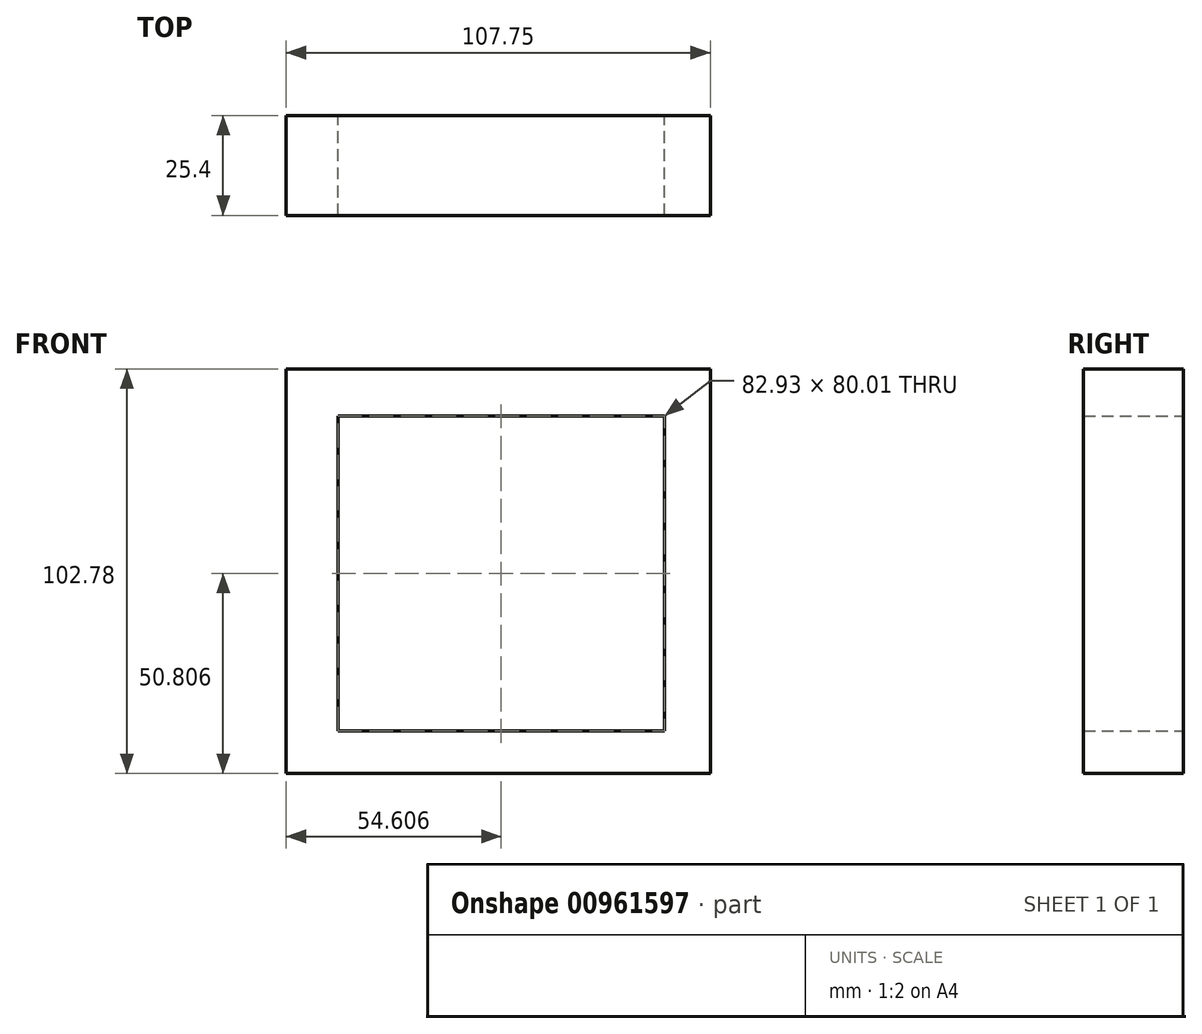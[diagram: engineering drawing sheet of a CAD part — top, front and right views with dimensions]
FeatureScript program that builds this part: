
annotation { "Feature Type Name" : "Feature", "Feature Type Description" : "" }
export const myFeature = defineFeature(function(context is Context, id is Id, definition is map)
    precondition{}
    {
        {
            var Q0;
            Q0=qCreatedBy(makeId("Front.planeOp"),FACE);
            var sketch = newSketch(context, id + "F0", { "sketchPlane" : qUnion([Q0])});
            skLineSegment(sketch, "E0.bottom", {"start": v(0, 55.04) * mm, "end": v(-55.92, 55.04) * mm});
            skLineSegment(sketch, "E0.top", {"start": v(0, -47.74) * mm, "end": v(-55.92, -47.74) * mm});
            skLineSegment(sketch, "E0.left", {"start": v(0, 55.04) * mm, "end": v(0, -47.74) * mm});
            skLineSegment(sketch, "E0.right", {"start": v(-55.92, 55.04) * mm, "end": v(-55.92, -47.74) * mm});
            skPoint(sketch, "E1.oppositeSnap0", {"position": v(-27.96, -47.74) * mm});
            skLineSegment(sketch, "E1.bottom", {"start": v(0, 55.04) * mm, "end": v(51.83, 55.04) * mm});
            skLineSegment(sketch, "E1.top", {"start": v(0, -47.74) * mm, "end": v(51.83, -47.74) * mm});
            skLineSegment(sketch, "E1.right", {"start": v(51.83, 55.04) * mm, "end": v(51.83, -47.74) * mm});
            skLineSegment(sketch, "E2.bottom", {"start": v(0, 43.07) * mm, "end": v(-42.78, 43.07) * mm});
            skLineSegment(sketch, "E2.top", {"start": v(0, -36.94) * mm, "end": v(-42.78, -36.94) * mm});
            skLineSegment(sketch, "E2.left", {"start": v(0, 43.07) * mm, "end": v(0, -36.94) * mm});
            skLineSegment(sketch, "E2.right", {"start": v(-42.78, 43.07) * mm, "end": v(-42.78, -36.94) * mm});
            skLineSegment(sketch, "E3.bottom", {"start": v(0, 43.07) * mm, "end": v(40.15, 43.07) * mm});
            skLineSegment(sketch, "E3.top", {"start": v(0, -36.94) * mm, "end": v(40.15, -36.94) * mm});
            skLineSegment(sketch, "E3.right", {"start": v(40.15, 43.07) * mm, "end": v(40.15, -36.94) * mm});
            skSolve(sketch);
        }
        {
            var Q0;
            {var subQ2=sQuery(id+"F0.wireOp",EDGE,"E0.bottom");Q0=makeQuery(id+"F0.imprint","IMPRINT",FACE,{"disambiguationData":[TD([[makeQuery(id+"F0.imprint","IMPRINT",EDGE,{"derivedFrom":subQ2}),1.0]])]});}
            var Q1;
            {var subQ4=sQuery(id+"F0.wireOp",EDGE,"E1.bottom");Q1=makeQuery(id+"F0.imprint","IMPRINT",FACE,{"disambiguationData":[TD([[makeQuery(id+"F0.imprint","IMPRINT",EDGE,{"derivedFrom":subQ4}),-1.0]])]});}
            extrude(context, id + "F1", {"entities" : qUnion([Q0, Q1]), "depth" : 25.4 * mm, "offsetDistance" : 25.4 * mm});
        }
    });
